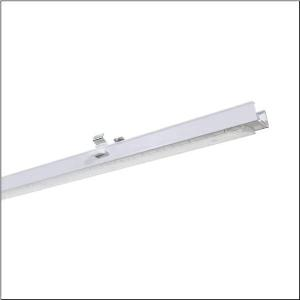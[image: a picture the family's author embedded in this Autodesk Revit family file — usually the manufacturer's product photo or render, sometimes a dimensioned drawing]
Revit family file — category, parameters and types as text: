
# Revit family: trunking_flex_31_51re18ma46b
name_source: partatom
category: Lighting Fixtures
units: mm (PartAtom-declared; Revit-internal decimal feet)

## family parameters
Cut with Voids When Loaded = No
Host = Face
Light Source = No
Part Type = Normal
Room Calculation Point = No
Round Connector Dimension = Use Diameter
Shared = No

## types (1)
- --- (1 x LED, 6400 lm, 40 W, 4000K)
    Apparent Load = 40 VA
    CIE Flux Codes = 71 89 97 97 100
    Color Rendering = 80
    Color Temperature = 4000K
    Default Elevation = 1800 mm
    Description = Trunking Flex 31, luminaire insert, of extruded aluminium section, coated, traffic white (RAL 9016), length: 1.172mm, width: 91mm, height: 53mm, LED rated luminous flux: 6.400lm, light colour: 840, control gear: ON/OFF Multilumen, with system connector: socket, mains connection: 220..240V, AC, 50/60Hz, rated input power: 40W, luminous flux adjustable on luminaire in four steps (3420/4540/5580/6630lm), connected load according to luminous flux setting (20/26/33/40W), primary light control with lens, of plastic, primary optical cover: cover, of PMMA, light emission: direct distribution, protection rating (complete): IP20, insulation class (complete): insulation class I (protective earthing), certification: CE, UKCA, impact resistance: IK02, permissible ambient temperature for indoor applications: -20..+40°C, packaging unit: 1 piece
    Height = 58 mm
    Lamp = 1 x LED
    Lamp Light Flux = 6400 lm
    Lamp Power = 40 W
    Lamp count = 1
    Length = 1172 mm
    Luminous efficacy = 160 lm/W
    Manufacturer = Siteco
    ModVariant = No
    Model = 51RE18MA46B
    Mounting Place = Ceiling
    Mounting Type = Pendant
    Number of Poles = 1
    OnlyDefault = Yes
    Power Factor = 1
    Product Name = Trunking Flex 31
    Product group = luminaire insert
    ProductGroupID = 901
    Protection Class = Protection class I
    Protection Degree = IP 20
    RLX_Detail_Level = 1
    RLX_Emergency_Light_Flux = 0 lm
    RLX_Emergency_Type = 0
    RLX_Emergency_Type_DB = No
    RlxData = <blob elided: 20053 chars, md5=cfeff958>
    Socket = socket
    Standby Power = 0 W
    System Light Flux = 6400 lm
    System Power = 40 W
    Type Comments = factory setting: luminous flux: 100 % | (ON | ON) | 300 mA
    Type Image = l_1266702.jpg
    URL = http://relux.com
    VarID = @adj_001217
    Voltage = 0 V
    Weight = 0.00 kg
    Width = 65 mm

## geometry (parser evidence)
native form markers: Blend x4, Sweep x12
no freeform markers — native parametric forms only
